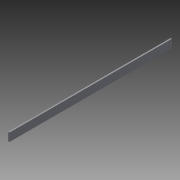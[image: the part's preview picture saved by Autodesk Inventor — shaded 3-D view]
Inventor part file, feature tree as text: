
AUTODESK INVENTOR PART (.ipt)
format: ipt  version: 2015 SP1 (Build 190203100, 203)  size: 77,824 bytes
history: native  units: mm
features: other x3, sketch x1
ambient origin geometry x8: Origin, YZ Plane, XZ Plane, XY Plane, X Axis, Y Axis, Z Axis, Center Point
bodies: Solid1 (feature_tree)
feature tree (4):
  other  "Mirroir.ipt"
  other  "Solid1::Mirroir.ipt"
  other  "TaggingFeature1"
  sketch  "Sketch1"  dims[d0=10.0mm]
